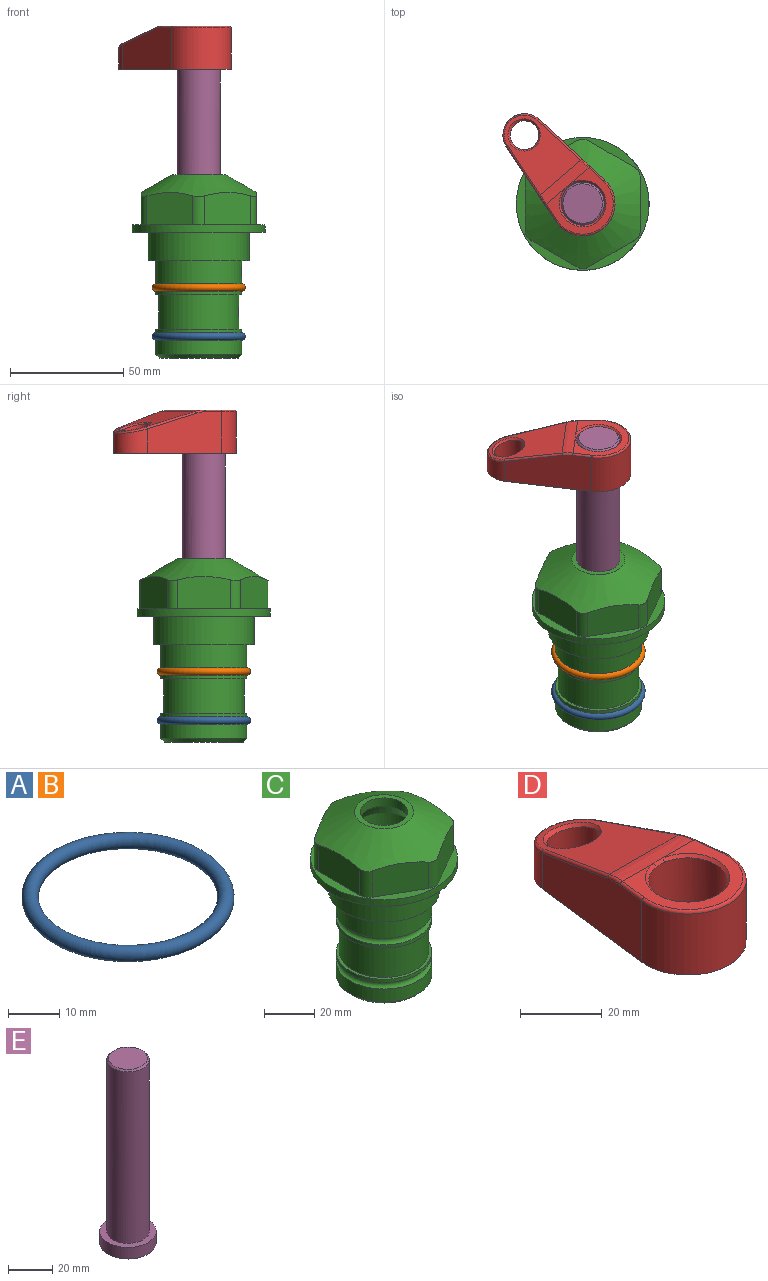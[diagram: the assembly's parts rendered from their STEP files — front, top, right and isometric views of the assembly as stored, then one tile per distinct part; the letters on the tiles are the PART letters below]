
ASSEMBLY  parts=5 mates=4
PART A: 1 faces, bbox 44.7x44.7x3.2 mm
  f0: torus R=19.05mm, axis (0,0,1), area 1193.9mm2
PART B: same geometry as A
PART C: 36 faces, bbox 58.7x58.7x81 mm
  f0: cylinder r=17.78mm len=35.56mm, axis (0,0,1), area 1670.8mm2, adj f23,f24,f31
  f1: cylinder r=19.05mm len=38.1mm, axis (0,0,1), area 1191.9mm2, adj f26,f27,f30
  f2: plane 58.66x58.66mm, normal (0,0,-1), area 1150.6mm2, adj f3,f28
  f3: cylinder r=29.33mm len=58.66mm, axis (0,0,-1), area 585.1mm2, adj f2,f4
  f4: plane 58.66x58.66mm, normal (0,0,1), area 475.9mm2, adj f3,f5,f6,f7,f8,f9,f10,f11
  f5: plane 20.32x14.34mm, normal (-0.5,0.87,0), area 324.4mm2, adj f4,f15,f16,f17
  f6: plane 20.32x14.34mm, normal (0.5,0.87,0), area 324.4mm2, adj f4,f14,f15,f17
  f7: plane 23.48x14.34mm, normal (1,0,0), area 324.4mm2, adj f4,f13,f14,f17
  f8: plane 20.32x14.34mm, normal (0.5,-0.87,0), area 324.4mm2, adj f4,f12,f13,f17
  f9: plane 20.32x14.34mm, normal (-0.5,-0.87,0), area 324.4mm2, adj f4,f11,f12,f17
  f10: plane 23.48x14.34mm, normal (-1,0,0), area 324.4mm2, adj f4,f11,f16,f17
  f11: cylinder r=5.08mm len=12.85mm, axis (0,0,-1), area 67.2mm2, adj f4,f9,f10,f17
  f12: cylinder r=5.08mm len=12.85mm, axis (0,0,-1), area 67.2mm2, adj f4,f8,f9,f17
  f13: cylinder r=5.08mm len=12.85mm, axis (0,0,-1), area 67.2mm2, adj f4,f7,f8,f17
  f14: cylinder r=5.08mm len=12.85mm, axis (0,0,-1), area 67.2mm2, adj f4,f6,f7,f17
  f15: cylinder r=5.08mm len=12.85mm, axis (0,0,-1), area 67.2mm2, adj f4,f5,f6,f17
  f16: cylinder r=5.08mm len=12.85mm, axis (0,0,-1), area 67.2mm2, adj f4,f5,f10,f17
  f17: cone r=11.73mm half-angle=60deg, axis (0,0,-1), area 2071.8mm2, adj f5,f6,f7,f8,f9,f10,f11,f12
  f18: plane 23.46x23.46mm, normal (0,0,1), area 147.4mm2, adj f17,f35
  f19: plane 34.93x34.93mm, normal (0,0,-1), area 958mm2, adj f29
  f20: cylinder r=19.05mm len=38.1mm, axis (0,0,1), area 760.1mm2, adj f21,f29
  f21: torus R=19.05mm, axis (0,0,1), area 565.3mm2, adj f20,f22
  f22: cylinder r=19.05mm len=38.1mm, axis (0,0,1), area 190mm2, adj f21,f23
  f23: plane 38.1x38.1mm, normal (0,0,1), area 146.9mm2, adj f0,f22
  f24: plane 38.1x38.1mm, normal (0,0,-1), area 146.9mm2, adj f0,f25
  f25: cylinder r=19.05mm len=38.1mm, axis (0,0,1), area 190mm2, adj f24,f26
  f26: torus R=19.05mm, axis (0,0,1), area 565.3mm2, adj f1,f25
  f27: plane 44.45x44.45mm, normal (0,0,-1), area 411.7mm2, adj f1,f28
  f28: cylinder r=22.23mm len=44.45mm, axis (0,0,1), area 1773.5mm2, adj f2,f27
  f29: cone r=19.05mm half-angle=45deg, axis (0,0,1), area 257.5mm2, adj f19,f20
  f30: cylinder r=3.17mm len=6.75mm, axis (-1,0,0), area 128mm2, adj f1,f33
  f31: cylinder r=3.17mm len=6.35mm, axis (-1,0,0), area 102.5mm2, adj f0,f33
  f32: plane 25.4x25.4mm, normal (0,0,1), area 506.7mm2, adj f33
  f33: cylinder r=12.7mm len=66.42mm, axis (0,0,-1), area 5236.2mm2, adj f30,f31,f32,f34
  f34: cone r=9.53mm half-angle=30deg, axis (0,0,-1), area 443.4mm2, adj f33,f35
  f35: cylinder r=9.53mm len=19.05mm, axis (0,0,-1), area 240.9mm2, adj f18,f34
PART D: 31 faces, bbox 31.7x65.5x19.8 mm
  f0: plane 39.12x18.26mm, normal (0.99,0.12,0), area 612.2mm2, adj f1,f4,f7,f11,f13,f15
  f1: cylinder r=9.53mm len=18.91mm, axis (0,0,-1), area 296.1mm2, adj f0,f2,f7,f17
  f2: plane 39.12x18.26mm, normal (-0.99,0.12,0), area 612.2mm2, adj f1,f4,f7,f12,f14,f16
  f3: cylinder r=6.35mm len=12.7mm, axis (0,0,-1), area 362.4mm2, adj f7,f18
  f4: cylinder r=14.29mm len=28.58mm, axis (0,0,-1), area 882.2mm2, adj f0,f2,f7,f10
  f5: cylinder r=9.53mm len=19.05mm, axis (0,0,-1), area 1092.6mm2, adj f7,f19,f20
  f6: plane 26.99x23.69mm, normal (0,0,1), area 216.2mm2, adj f9,f10,f11,f12,f19
  f7: plane 63.5x28.58mm, normal (0,0,-1), area 661.8mm2, adj f0,f1,f2,f3,f4,f5,f22,f23
  f8: plane 33.52x23.6mm, normal (0,0.26,0.97), area 486mm2, adj f9,f15,f16,f17,f18
  f9: cylinder r=19.05mm len=24.72mm, axis (1,0,0), area 120.4mm2, adj f6,f8,f13,f14,f20
  f10: torus R=13.49mm, axis (0,0,1), area 59mm2, adj f4,f6,f11,f12
  f11: cylinder r=0.79mm len=8.67mm, axis (0.12,-0.99,0), area 10.8mm2, adj f0,f6,f10,f13
  f12: cylinder r=0.79mm len=8.67mm, axis (0.12,0.99,0), area 10.8mm2, adj f2,f6,f10,f14
  f13: bspline ~4.95x1.42mm, area 6.1mm2, adj f0,f9,f11,f15
  f14: bspline ~4.95x1.42mm, area 6.1mm2, adj f2,f9,f12,f16
  f15: cylinder r=0.79mm len=25.95mm, axis (0.12,-0.96,0.26), area 32.9mm2, adj f0,f8,f13,f17
  f16: cylinder r=0.79mm len=25.95mm, axis (0.12,0.96,-0.26), area 32.9mm2, adj f2,f8,f14,f17
  f17: bspline ~18.91x8.38mm, area 30mm2, adj f1,f8,f15,f16
  f18: bspline ~14.29x14.29mm, area 48.3mm2, adj f3,f8
  f19: cone r=9.53mm half-angle=45deg, axis (0,0,1), area 66.5mm2, adj f5,f6,f20
  f20: bspline ~3.22x0.96mm, area 3.5mm2, adj f5,f9,f19
  f21: plane 2.75x2.72mm, normal (0,0,-1), area 2.9mm2, adj f23,f25,f28
  f22: plane 23.05x15.88mm, normal (-0.99,-0.12,0), area 323.6mm2, adj f7,f25,f26,f27,f28,f29
  f23: plane 23.05x15.88mm, normal (0.99,-0.12,0), area 323.6mm2, adj f7,f21,f25,f27,f28,f30
  f24: cylinder r=9.53mm len=10.69mm, axis (0,0,-1), area 114.7mm2, adj f7,f27,f29,f30
  f25: cylinder r=12.7mm len=20.59mm, axis (0,0,-1), area 381.1mm2, adj f7,f21,f22,f23,f26,f28
  f26: plane 2.75x2.72mm, normal (0,0,-1), area 2.9mm2, adj f22,f25,f28
  f27: plane 19.72x18.37mm, normal (0,-0.26,-0.97), area 291.8mm2, adj f22,f23,f24,f28,f29,f30
  f28: cylinder r=15.88mm len=19.92mm, axis (1,0,0), area 54.8mm2, adj f21,f22,f23,f25,f26,f27
  f29: cylinder r=1.59mm len=11mm, axis (0,0,-1), area 34.7mm2, adj f7,f22,f24,f27
  f30: cylinder r=1.59mm len=11mm, axis (0,0,-1), area 34.7mm2, adj f7,f23,f24,f27
PART E: 6 faces, bbox 25.4x25.4x101.6 mm
  f0: plane 17.46x17.46mm, normal (0,0,1), area 239.5mm2, adj f5
  f1: plane 25.4x25.4mm, normal (0,0,-1), area 506.7mm2, adj f2
  f2: cylinder r=12.7mm len=25.4mm, axis (0,0,1), area 506.7mm2, adj f1,f3
  f3: plane 25.4x25.4mm, normal (0,0,1), area 221.7mm2, adj f2,f4
  f4: cylinder r=9.53mm len=94.46mm, axis (0,0,1), area 5653mm2, adj f3,f5
  f5: cone r=8.73mm half-angle=45deg, axis (0,0,-1), area 64.4mm2, adj f0,f4
PLACE A t=(0,0,-21.59)mm
PLACE B at identity
PLACE C at identity fixed
PLACE D rot(axis=(0,0,1),40.4deg) t=(0,0,27.55)mm
PLACE E rot(axis=(0,0,1),40.4deg) t=(0,0,27.55)mm
MATE fastened E.f2 <-> D.f4  axis (0,0,1) through (0,0,91.05)mm
MATE fastened B.f0 <-> C.f0  axis (0,0,1) through (0,0,-24.51)mm
MATE fastened A.f0 <-> C.f0  axis (0,0,1) through (0,0,-46.1)mm
MATE cylindrical C.f0 <-> E.f2  axis (0,0,-1) through (0,0,-50.55)mm
